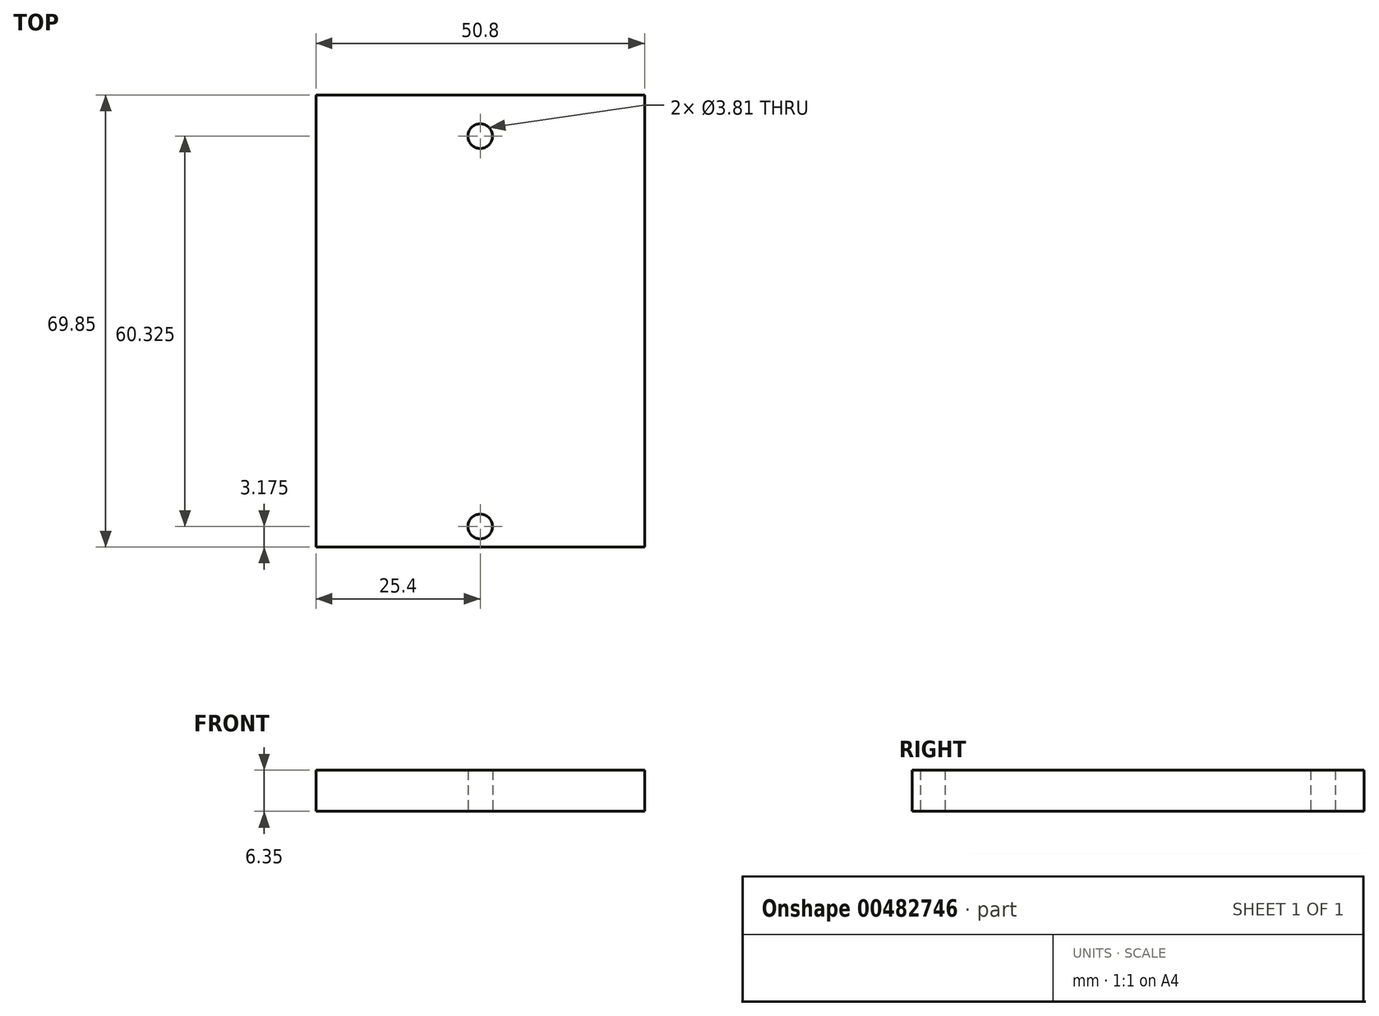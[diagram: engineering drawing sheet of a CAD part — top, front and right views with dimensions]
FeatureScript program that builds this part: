
annotation { "Feature Type Name" : "Feature", "Feature Type Description" : "" }
export const myFeature = defineFeature(function(context is Context, id is Id, definition is map)
    precondition{}
    {
        {
            var Q0;
            Q0=qCreatedBy(makeId("Top.planeOp"),FACE);
            var sketch = newSketch(context, id + "F0", { "sketchPlane" : qUnion([Q0])});
            skLineSegment(sketch, "E0", {"start": v(0, 39.41) * mm, "end": v(0, -31.75) * mm, "construction": true});
            skLineSegment(sketch, "E1.MirrorCS", {"start": v(25.4, 31.75) * mm, "end": v(25.4, -31.75) * mm, "construction": true});
            skLineSegment(sketch, "E2.0", {"start": v(14.37, 54.16) * mm, "end": v(14.37, -26.9) * mm, "construction": true});
            skPoint(sketch, "E3.orphan", {"position": v(25.4, -26.9) * mm});
            skPoint(sketch, "E4.orphan", {"position": v(-25.4, -26.9) * mm});
            skLineSegment(sketch, "E5.top", {"start": v(-25.4, -31.75) * mm, "end": v(25.4, -31.75) * mm});
            skCircle(sketch, "E6", {"center": v(0, 31.75) * mm, "radius": 1.9 * mm});
            skCircle(sketch, "E7", {"center": v(0, -28.58) * mm, "radius": 1.9 * mm});
            skLineSegment(sketch, "E8", {"start": v(-25.4, 25.4) * mm, "end": v(25.4, 25.4) * mm});
            skLineSegment(sketch, "E9", {"start": v(25.4, -25.4) * mm, "end": v(-25.4, -25.4) * mm});
            skLineSegment(sketch, "E10", {"start": v(-14.37, 38.1) * mm, "end": v(14.37, 38.1) * mm});
            skLineSegment(sketch, "E11.MirrorCS", {"start": v(-14.37, 54.16) * mm, "end": v(-14.37, -26.9) * mm, "construction": true});
            skLineSegment(sketch, "E12.trimOffspring", {"start": v(-25.4, 31.75) * mm, "end": v(-25.4, -31.75) * mm, "construction": true});
            skLineSegment(sketch, "E13.trimOffspring", {"start": v(25.4, 31.75) * mm, "end": v(25.4, -31.75) * mm});
            skLineSegment(sketch, "E14.trimOffspring", {"start": v(-25.4, 31.75) * mm, "end": v(-25.4, -31.75) * mm});
            skLineSegment(sketch, "E15", {"start": v(-14.37, 38.1) * mm, "end": v(-25.4, 38.1) * mm});
            skLineSegment(sketch, "E16", {"start": v(-25.4, 38.1) * mm, "end": v(-25.4, 31.75) * mm});
            skLineSegment(sketch, "E17", {"start": v(14.37, 38.1) * mm, "end": v(25.4, 38.1) * mm});
            skLineSegment(sketch, "E18", {"start": v(25.4, 38.1) * mm, "end": v(25.4, 31.75) * mm});
            skSolve(sketch);
        }
        {
            var Q0;
            {var subQ0=sQuery(id+"F0.wireOp",EDGE,"E8");Q0=makeQuery(id+"F0.imprint","IMPRINT",FACE,{"disambiguationData":[TD([[makeQuery(id+"F0.imprint","IMPRINT",EDGE,{"derivedFrom":subQ0}),-1.0]])]});}
            var Q1;
            Q1=makeQuery(id+"F0.imprint","IMPRINT",FACE,{"disambiguationData":[TD([[makeQuery(id+"F0.imprint","IMPRINT",EDGE,{"derivedFrom":sQuery(id+"F0.wireOp",EDGE,"E6")}),-1.0]])]});
            var Q2;
            {var subQ1=sQuery(id+"F0.wireOp",EDGE,"E5.top");Q2=makeQuery(id+"F0.imprint","IMPRINT",FACE,{"disambiguationData":[TD([[makeQuery(id+"F0.imprint","IMPRINT",EDGE,{"derivedFrom":subQ1}),1.0]])]});}
            extrude(context, id + "F1", {"entities" : qUnion([Q0, Q1, Q2]), "depth" : 6.35 * mm});
        }
    });
